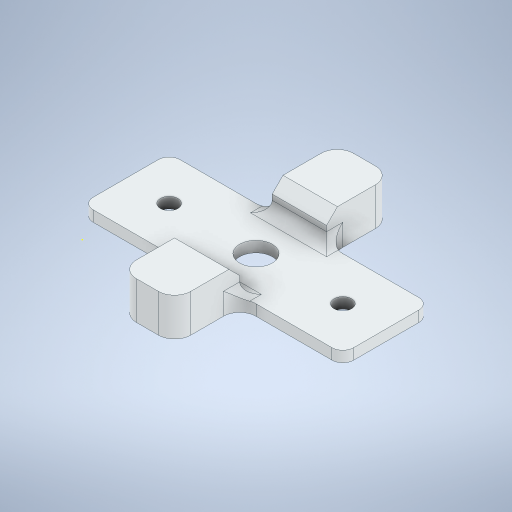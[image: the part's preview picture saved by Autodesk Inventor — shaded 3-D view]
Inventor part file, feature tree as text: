
AUTODESK INVENTOR PART (.ipt)
format: ipt  version: 2024 (Build 280153000, 153)  size: 645,632 bytes
history: native  units: in
note: dims shown in document units (in); Inventor stores cm internally (conversion verified against a paired STEP export)
features: sketch x22, extrude x21, projected_geometry x12, fillet x4, chamfer x1
ambient origin geometry x8: Origin, YZ Plane, XZ Plane, XY Plane, X Axis, Y Axis, Z Axis, Center Point
bodies: Solid1 (feature_tree)
feature tree (60):
  sketch  "Sketch1"  dims[d0=47.6875in d1=0.0in d2=1.5in]
  extrude  "Extrusion1"  Depth=1.5in
  extrude  "Extrusion2"  Depth=0.344in
  extrude  "Extrusion3"  Depth=0.344in
  extrude  "Extrusion4"  Depth=0.17in
  extrude  "Extrusion5"  Depth=0.3594in TaperAngle=0.0deg
  extrude  "Extrusion6"  Depth=0.125in
  extrude  "Extrusion7"  Depth=1.0in TaperAngle=0.0deg
  extrude  "Extrusion8"  Depth=0.125in
  sketch  "Sketch13"  dims[d33=1.0in d34=2.7031in d35=0.0in]
  extrude  "Extrusion9"  Depth=1.3594in TaperAngle=0.0deg
  extrude  "Extrusion10"  Depth=1.0in TaperAngle=0.0deg
  extrude  "Extrusion11"  Depth=0.1094in TaperAngle=0.0deg
  extrude  "Extrusion12"  Depth=0.1875in TaperAngle=0.0deg
  fillet  "Fillet3"  Radius=0.1875in
  extrude  "Extrusion13"  Depth=0.375in
  extrude  "Extrusion14"  Depth=0.951in
  extrude  "Extrusion15"  Depth=0.1875in TaperAngle=0.0deg
  extrude  "Extrusion16"  Depth=0.5in TaperAngle=0.0deg
  sketch  "Sketch22"  dims[d68=0.125in d69=0.0625in d70=0.0in d71=0.0625in d72=0.0in]
  extrude  "Extrusion17"  Depth=0.125in TaperAngle=0.0deg
  extrude  "Extrusion18"  Depth=0.125in TaperAngle=0.0deg
  extrude  "Extrusion19"  Depth=0.0625in TaperAngle=0.0deg
  fillet  "Fillet5"  Radius=0.0625in
  extrude  "Extrusion21"  Depth=0.125in TaperAngle=45.0deg
  extrude  "Extrusion22"  [1 undecoded]
  fillet  "Fillet6"  [1 undecoded]
  chamfer  "Chamfer1"  [1 undecoded]
  sketch  "Sketch2"  dims[d3=0.375in d4=0.344in]
  sketch  "Sketch3"  dims[d5=6.4375in d6=0.0in d7=0.344in]
  sketch  "Sketch5"  dims[d8=0.17in d9=0.17in]
  sketch  "Sketch7"  dims[d10=0.3594in d11=0.0in d12=0.3594in d13=0.0in]
  projected_geometry  "Projected Loop1"
  sketch  "Sketch8"  dims[d14=0.1249in d15=0.125in]
  sketch  "Sketch9"  dims[d16=1.0in d17=1.0781in d18=0.0in]
  sketch  "Sketch10"  dims[d19=1.103in d28=0.125in]
  projected_geometry  "Projected Loop2"
  sketch  "Sketch12"  dims[d29=1.0781in d30=0.0in d31=1.3594in d32=0.0in]
  sketch  "Sketch14"  dims[d36=0.9844in d37=0.0in d38=0.1094in d39=0.0in]
  projected_geometry  "Projected Loop4"
  sketch  "Sketch15"  dims[d41=0.75in d42=0.0in d43=0.75in d44=0.0in d45=0.1875in]
  projected_geometry  "Projected Loop5"
  sketch  "Sketch16"  dims[d46=0.375in d47=0.375in]
  sketch  "Sketch17"  dims[d48=0.9511in d49=0.951in]
  sketch  "Sketch18"  dims[d50=0.1875in d51=0.0in d52=1.4375in d53=0.0in]
  sketch  "Sketch19"  dims[d54=0.875in d55=0.0in d56=0.5in d57=0.0in]
  projected_geometry  "Projected Loop6"
  sketch  "Sketch20"  dims[d58=0.375in d59=0.125in d60=0.0in]
  projected_geometry  "Projected Loop7"
  sketch  "Sketch21"  dims[d61=0.125in d62=0.0in d63=0.187in d64=0.0in]
  projected_geometry  "Projected Loop8"
  sketch  "Sketch23"  dims[d73=0.125in d74=0.125in d75=0.125in d76=45.0deg]
  projected_geometry  "Projected Loop9"
  sketch  "Sketch25"
  projected_geometry  "Projected Loop12"
  projected_geometry  "Projected Loop13"
  sketch  "Sketch26"
  projected_geometry  "Projected Loop14"
  projected_geometry  "Projected Loop15"
  fillet  "Fillet2"  [1 undecoded]
note: 4 required parameter values undecoded (feature->parameter linkage not recoverable at this tier; creation-order binding heuristic only, values carry confidence <= 0.55)
